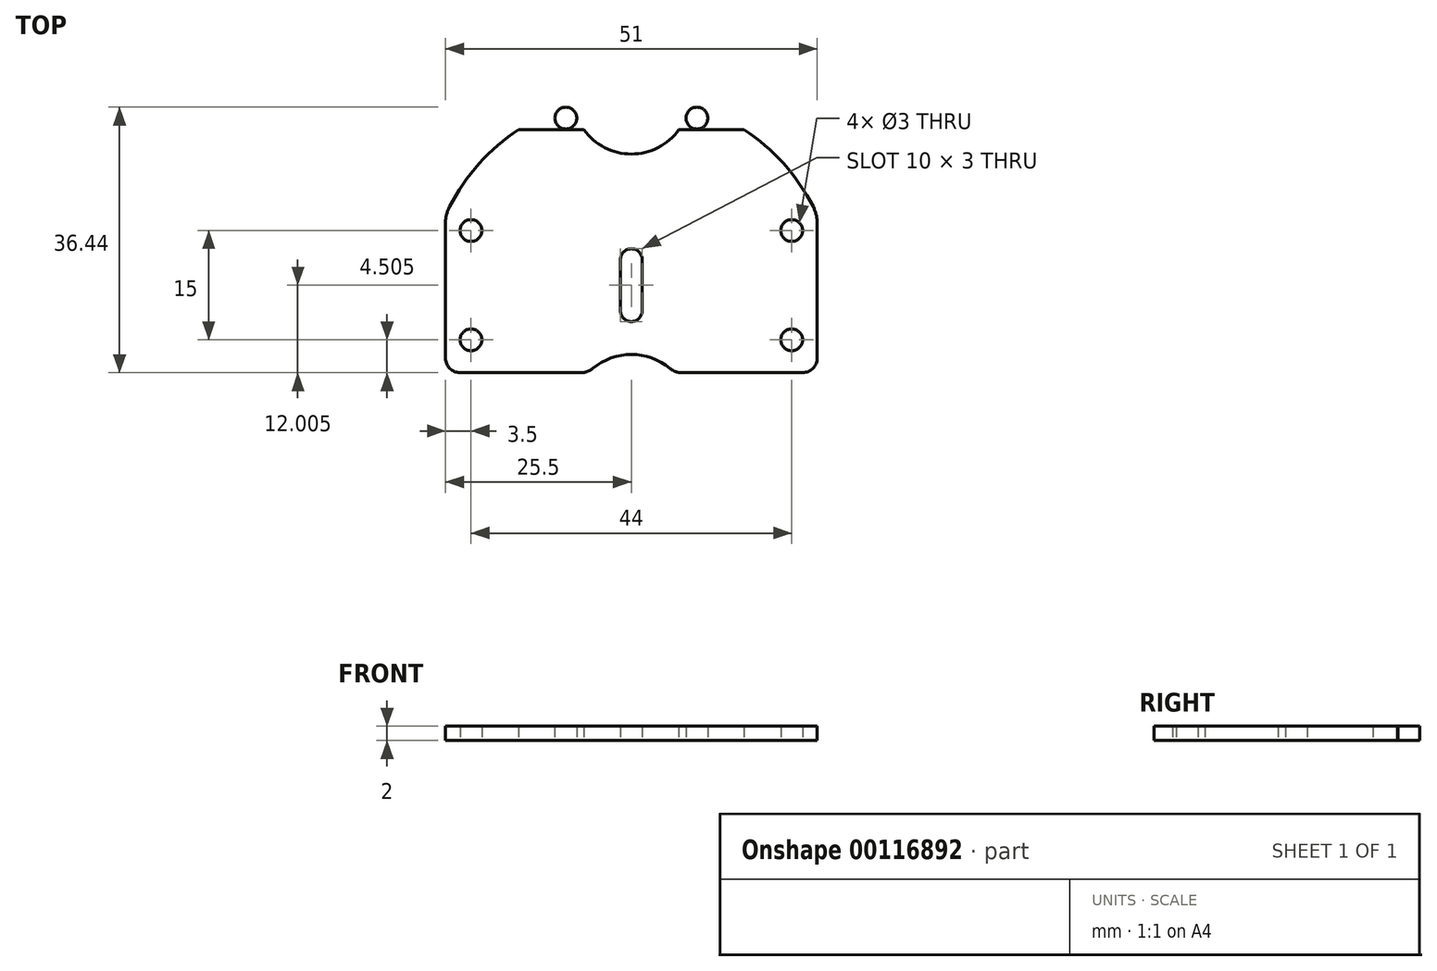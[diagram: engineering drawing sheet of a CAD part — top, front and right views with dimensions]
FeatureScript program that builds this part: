
annotation { "Feature Type Name" : "Feature", "Feature Type Description" : "" }
export const myFeature = defineFeature(function(context is Context, id is Id, definition is map)
    precondition{}
    {
        {
            var Q0;
            Q0=qCreatedBy(makeId("Top.planeOp"),FACE);
            var sketch = newSketch(context, id + "F0", { "sketchPlane" : qUnion([Q0])});
            skLineSegment(sketch, "E0", {"start": v(-27.15, 153.46) * mm, "end": v(-17.3, 155.2) * mm});
            skLineSegment(sketch, "E1", {"start": v(-17.3, 155.2) * mm, "end": v(-14.87, 141.4) * mm});
            skLineSegment(sketch, "E2", {"start": v(-14.87, 141.4) * mm, "end": v(-24.72, 139.67) * mm});
            skLineSegment(sketch, "E3", {"start": v(-24.72, 139.67) * mm, "end": v(-27.15, 153.46) * mm});
            skLineSegment(sketch, "E4", {"start": v(-8.87, 175.2) * mm, "end": v(-8.87, 29.62) * mm});
            skLineSegment(sketch, "E5", {"start": v(-63.87, 175.2) * mm, "end": v(-63.87, 29.62) * mm});
            skCircle(sketch, "E6", {"center": v(-17.3, 155.2) * mm, "radius": 1.43 * mm});
            skCircle(sketch, "E7", {"center": v(-27.15, 153.46) * mm, "radius": 1.43 * mm});
            skCircle(sketch, "E8", {"center": v(-24.72, 139.67) * mm, "radius": 1.43 * mm});
            skCircle(sketch, "E9", {"center": v(-14.87, 141.4) * mm, "radius": 1.43 * mm});
            skLineSegment(sketch, "E10", {"start": v(-63.87, 175.2) * mm, "end": v(-8.87, 175.2) * mm});
            skLineSegment(sketch, "E11", {"start": v(-45.6, 153.46) * mm, "end": v(-55.44, 155.2) * mm});
            skLineSegment(sketch, "E12", {"start": v(-55.44, 155.2) * mm, "end": v(-57.87, 141.4) * mm});
            skLineSegment(sketch, "E13", {"start": v(-57.87, 141.4) * mm, "end": v(-48.02, 139.67) * mm});
            skLineSegment(sketch, "E14", {"start": v(-48.02, 139.67) * mm, "end": v(-45.6, 153.46) * mm});
            skCircle(sketch, "E15", {"center": v(-55.44, 155.2) * mm, "radius": 1.43 * mm});
            skCircle(sketch, "E16", {"center": v(-45.6, 153.46) * mm, "radius": 1.43 * mm});
            skCircle(sketch, "E17", {"center": v(-48.02, 139.67) * mm, "radius": 1.43 * mm});
            skCircle(sketch, "E18", {"center": v(-57.87, 141.4) * mm, "radius": 1.43 * mm});
            skLineSegment(sketch, "E19", {"start": v(-36.37, 175.2) * mm, "end": v(-36.37, 125.26) * mm});
            skPoint(sketch, "E20", {"position": v(-36.37, 197.7) * mm});
            skArc(sketch, "E21", {"start": v(-11.42, 182.48) * mm, "mid": v(-36.37, 197.7) * mm, "end": v(-61.32, 182.48) * mm});
            skCircle(sketch, "E22", {"center": v(-36.37, 175.2) * mm, "radius": 1.5 * mm});
            skPoint(sketch, "E23.visualSharp", {"position": v(-63.87, 175.2) * mm});
            skPoint(sketch, "E24.visualSharp", {"position": v(-8.87, 175.2) * mm});
            skCircle(sketch, "E25", {"center": v(-58.87, 128.4) * mm, "radius": 1.5 * mm});
            skCircle(sketch, "E26.MirrorC", {"center": v(-13.87, 128.4) * mm, "radius": 1.5 * mm});
            skLineSegment(sketch, "E27", {"start": v(-48.87, 165.2) * mm, "end": v(-23.87, 165.2) * mm});
            skLineSegment(sketch, "E28", {"start": v(-53.87, 170.2) * mm, "end": v(-53.87, 191.57) * mm});
            skLineSegment(sketch, "E29", {"start": v(-18.87, 170.2) * mm, "end": v(-18.87, 191.57) * mm});
            skCircle(sketch, "E30", {"center": v(-56.37, 185.55) * mm, "radius": 2.5 * mm});
            skCircle(sketch, "E31", {"center": v(-16.37, 185.55) * mm, "radius": 2.5 * mm});
            skCircle(sketch, "E32", {"center": v(-58.37, 179.2) * mm, "radius": 1.5 * mm});
            skCircle(sketch, "E33", {"center": v(-14.37, 179.2) * mm, "radius": 1.5 * mm});
            skPoint(sketch, "E34.visualSharp", {"position": v(-53.87, 165.2) * mm});
            skArc(sketch, "E34.filletArc", {"start": v(-53.87, 170.2) * mm, "mid": v(-52.4, 166.66) * mm, "end": v(-48.87, 165.2) * mm});
            skPoint(sketch, "E35.visualSharp", {"position": v(-18.87, 165.2) * mm});
            skArc(sketch, "E35.filletArc", {"start": v(-23.87, 165.2) * mm, "mid": v(-20.33, 166.66) * mm, "end": v(-18.87, 170.2) * mm});
            skCircle(sketch, "E36", {"center": v(-36.37, 153.94) * mm, "radius": 3.25 * mm});
            skCircle(sketch, "E37", {"center": v(-46.8, 146.56) * mm, "radius": 1.43 * mm});
            skCircle(sketch, "E38.MirrorC", {"center": v(-25.93, 146.56) * mm, "radius": 1.43 * mm});
            skCircle(sketch, "E39", {"center": v(-58.37, 164.2) * mm, "radius": 1.5 * mm});
            skCircle(sketch, "E40", {"center": v(-14.37, 164.2) * mm, "radius": 1.5 * mm});
            skLineSegment(sketch, "E41", {"start": v(-61.87, 180.19) * mm, "end": v(-61.87, 161.7) * mm});
            skLineSegment(sketch, "E42", {"start": v(-59.87, 159.7) * mm, "end": v(-12.87, 159.7) * mm});
            skLineSegment(sketch, "E43", {"start": v(-10.87, 161.7) * mm, "end": v(-10.87, 180.19) * mm});
            skCircle(sketch, "E44", {"center": v(-36.37, 153.94) * mm, "radius": 8.25 * mm});
            skLineSegment(sketch, "E45", {"start": v(-58.78, 188.05) * mm, "end": v(-8.48, 188.05) * mm});
            skArc(sketch, "E46.filletArc", {"start": v(-61.32, 182.48) * mm, "mid": v(-61.73, 181.37) * mm, "end": v(-61.87, 180.19) * mm});
            skArc(sketch, "E47.filletArc", {"start": v(-10.87, 180.19) * mm, "mid": v(-11.01, 181.37) * mm, "end": v(-11.42, 182.48) * mm});
            skPoint(sketch, "E48.visualSharp", {"position": v(-10.87, 159.7) * mm});
            skArc(sketch, "E48.filletArc", {"start": v(-12.87, 159.7) * mm, "mid": v(-11.46, 160.28) * mm, "end": v(-10.87, 161.7) * mm});
            skPoint(sketch, "E49.visualSharp", {"position": v(-61.87, 159.7) * mm});
            skArc(sketch, "E49.filletArc", {"start": v(-61.87, 161.7) * mm, "mid": v(-61.28, 160.28) * mm, "end": v(-59.87, 159.7) * mm});
            skCircle(sketch, "E50", {"center": v(-43.26, 162.2) * mm, "radius": 2.5 * mm});
            skCircle(sketch, "E51", {"center": v(-29.48, 162.2) * mm, "radius": 2.5 * mm});
            skLineSegment(sketch, "E52", {"start": v(-59.41, 193.05) * mm, "end": v(-9.71, 193.05) * mm});
            skCircle(sketch, "E53", {"center": v(-36.37, 197.7) * mm, "radius": 8 * mm});
            skCircle(sketch, "E54", {"center": v(-45.36, 194.63) * mm, "radius": 1.5 * mm});
            skCircle(sketch, "E55", {"center": v(-27.38, 194.63) * mm, "radius": 1.5 * mm});
            skCircle(sketch, "E56", {"center": v(-36.37, 168.2) * mm, "radius": 1.5 * mm});
            skLineSegment(sketch, "E57", {"start": v(-37.87, 177.83) * mm, "end": v(-37.87, 165.8) * mm});
            skLineSegment(sketch, "E58", {"start": v(-34.87, 178) * mm, "end": v(-34.87, 166.07) * mm});
            skSolve(sketch);
        }
        {
            var Q0;
            {var subQ46=sQuery(id+"F0.wireOp",EDGE,"E4");Q0=makeQuery(id+"F0.imprint","IMPRINT",FACE,{"disambiguationData":[TD([[makeQuery(id+"F0.imprint","IMPRINT",EDGE,{"derivedFrom":subQ46}),-1.0]])]});}
            var Q1;
            Q1=makeQuery(id+"F0.imprint","IMPRINT",FACE,{"disambiguationData":[TD([[makeQuery(id+"F0.imprint","IMPRINT",EDGE,{"derivedFrom":sQuery(id+"F0.wireOp",EDGE,"0QWr4Jdi-5Swy-qNiu-C7BZ-pfZC10sv86ri")}),-1.0]])]});
            var Q2;
            {var subQ3=sQuery(id+"F0.wireOp",EDGE,"zpIQ2hdJ-70NU-OBih-8Bg3-goN3WX9r9ZsD");var subQ13=sQuery(id+"F0.wireOp",EDGE,"KCor8Cqw-w0U3-ZJtW-jTcY-G1uKAieuV0Lt");var subQ14=makeQuery(id+"F0.imprint","INTERSECT",VERTEX,{"derivedFrom":[subQ13,subQ3]});Q2=makeQuery(id+"F0.imprint","IMPRINT",FACE,{"disambiguationData":[TD([[makeQuery(id+"F0.imprint","IMPRINT",EDGE,{"disambiguationData":[TD([[subQ14,-1.0]])],"derivedFrom":subQ13}),-1.0]])]});}
            var Q3;
            {var subQ3=sQuery(id+"F0.wireOp",EDGE,"xyZ8QybP-hO6P-4geZ-8f6D-PIsMQULHAIPK");var subQ5=sQuery(id+"F0.wireOp",EDGE,"mBHuYMz8-ZQLY-wNrG-rzVk-AeopOfV37pT8");var subQ6=makeQuery(id+"F0.imprint","INTERSECT",VERTEX,{"derivedFrom":[subQ5,subQ3]});Q3=makeQuery(id+"F0.imprint","IMPRINT",FACE,{"disambiguationData":[TD([[makeQuery(id+"F0.imprint","IMPRINT",EDGE,{"disambiguationData":[TD([[subQ6,-1.0]])],"derivedFrom":subQ5}),-1.0]])]});}
            var Q4;
            Q4=makeQuery(id+"F0.imprint","IMPRINT",FACE,{"disambiguationData":[TD([[makeQuery(id+"F0.imprint","IMPRINT",EDGE,{"derivedFrom":sQuery(id+"F0.wireOp",EDGE,"0QWr4Jdi-5Swy-qNiu-C7BZ-pfZC10sv86ri")}),1.0]])]});
            var Q5;
            Q5=makeQuery(id+"F0.imprint","IMPRINT",FACE,{"disambiguationData":[TD([[makeQuery(id+"F0.imprint","IMPRINT",EDGE,{"derivedFrom":sQuery(id+"F0.wireOp",EDGE,"fiuo85jt-HlLJ-ANnF-wLPQ-esjs3jnNE0SC")}),1.0]])]});
            var Q6;
            Q6=makeQuery(id+"F0.imprint","IMPRINT",FACE,{"disambiguationData":[TD([[makeQuery(id+"F0.imprint","IMPRINT",EDGE,{"derivedFrom":sQuery(id+"F0.wireOp",EDGE,"nJGxZEk8-BIZM-s0Uf-ehRU-cHSEgP5oKWdw")}),1.0]])]});
            var Q7;
            Q7=makeQuery(id+"F0.imprint","IMPRINT",FACE,{"disambiguationData":[TD([[makeQuery(id+"F0.imprint","IMPRINT",EDGE,{"derivedFrom":sQuery(id+"F0.wireOp",EDGE,"yOxkreaX-tzGu-CvLJ-NVHy-oeYss2fHvc5B")}),1.0]])]});
            var Q8;
            {var subQ0=sQuery(id+"F0.wireOp",EDGE,"Asq052DE-T6gE-0AAR-ghXs-JX1L81zWd4of");var subQ1=sQuery(id+"F0.wireOp",EDGE,"mBHuYMz8-ZQLY-wNrG-rzVk-AeopOfV37pT8");var subQ2=makeQuery(id+"F0.imprint","INTERSECT",VERTEX,{"derivedFrom":[subQ1,subQ0]});Q8=makeQuery(id+"F0.imprint","IMPRINT",FACE,{"disambiguationData":[TD([[makeQuery(id+"F0.imprint","IMPRINT",EDGE,{"disambiguationData":[TD([[subQ2,-1.0]])],"derivedFrom":subQ1}),1.0]])]});}
            var Q9;
            {var subQ0=sQuery(id+"F0.wireOp",EDGE,"Asq052DE-T6gE-0AAR-ghXs-JX1L81zWd4of");var subQ1=sQuery(id+"F0.wireOp",EDGE,"mBHuYMz8-ZQLY-wNrG-rzVk-AeopOfV37pT8");var subQ2=makeQuery(id+"F0.imprint","INTERSECT",VERTEX,{"derivedFrom":[subQ1,subQ0]});Q9=makeQuery(id+"F0.imprint","IMPRINT",FACE,{"disambiguationData":[TD([[makeQuery(id+"F0.imprint","IMPRINT",EDGE,{"disambiguationData":[TD([[subQ2,-1.0]])],"derivedFrom":subQ1}),-1.0]])]});}
            var Q10;
            {var subQ0=sQuery(id+"F0.wireOp",EDGE,"Asq052DE-T6gE-0AAR-ghXs-JX1L81zWd4of");var subQ1=sQuery(id+"F0.wireOp",EDGE,"4mQizIiY-woOy-cA2D-KRvu-nd4lGExxEz3w");var subQ2=makeQuery(id+"F0.imprint","INTERSECT",VERTEX,{"derivedFrom":[subQ1,subQ0]});Q10=makeQuery(id+"F0.imprint","IMPRINT",FACE,{"disambiguationData":[TD([[makeQuery(id+"F0.imprint","IMPRINT",EDGE,{"disambiguationData":[TD([[subQ2,1.0]])],"derivedFrom":subQ1}),1.0]])]});}
            var Q11;
            {var subQ0=sQuery(id+"F0.wireOp",EDGE,"Asq052DE-T6gE-0AAR-ghXs-JX1L81zWd4of");var subQ1=sQuery(id+"F0.wireOp",EDGE,"4mQizIiY-woOy-cA2D-KRvu-nd4lGExxEz3w");var subQ2=makeQuery(id+"F0.imprint","INTERSECT",VERTEX,{"derivedFrom":[subQ1,subQ0]});Q11=makeQuery(id+"F0.imprint","IMPRINT",FACE,{"disambiguationData":[TD([[makeQuery(id+"F0.imprint","IMPRINT",EDGE,{"disambiguationData":[TD([[subQ2,1.0]])],"derivedFrom":subQ1}),-1.0]])]});}
            var Q12;
            {var subQ0=sQuery(id+"F0.wireOp",EDGE,"MDdCBIRf-hswZ-m4EO-fIZG-vuCMY65TxToA");var subQ1=sQuery(id+"F0.wireOp",EDGE,"KCor8Cqw-w0U3-ZJtW-jTcY-G1uKAieuV0Lt");var subQ2=makeQuery(id+"F0.imprint","INTERSECT",VERTEX,{"derivedFrom":[subQ1,subQ0]});Q12=makeQuery(id+"F0.imprint","IMPRINT",FACE,{"disambiguationData":[TD([[makeQuery(id+"F0.imprint","IMPRINT",EDGE,{"disambiguationData":[TD([[subQ2,1.0]])],"derivedFrom":subQ1}),1.0]])]});}
            var Q13;
            {var subQ0=sQuery(id+"F0.wireOp",EDGE,"MDdCBIRf-hswZ-m4EO-fIZG-vuCMY65TxToA");var subQ1=sQuery(id+"F0.wireOp",EDGE,"KCor8Cqw-w0U3-ZJtW-jTcY-G1uKAieuV0Lt");var subQ2=makeQuery(id+"F0.imprint","INTERSECT",VERTEX,{"derivedFrom":[subQ1,subQ0]});Q13=makeQuery(id+"F0.imprint","IMPRINT",FACE,{"disambiguationData":[TD([[makeQuery(id+"F0.imprint","IMPRINT",EDGE,{"disambiguationData":[TD([[subQ2,1.0]])],"derivedFrom":subQ1}),-1.0]])]});}
            var Q14;
            {var subQ0=sQuery(id+"F0.wireOp",EDGE,"8OitHLvR-Y0PI-VGHX-yggo-vIoiIR1Yse0j");var subQ1=sQuery(id+"F0.wireOp",EDGE,"MDdCBIRf-hswZ-m4EO-fIZG-vuCMY65TxToA");var subQ2=makeQuery(id+"F0.imprint","INTERSECT",VERTEX,{"derivedFrom":[subQ1,subQ0]});Q14=makeQuery(id+"F0.imprint","IMPRINT",FACE,{"disambiguationData":[TD([[makeQuery(id+"F0.imprint","IMPRINT",EDGE,{"disambiguationData":[TD([[subQ2,1.0]])],"derivedFrom":subQ1}),1.0]])]});}
            var Q15;
            {var subQ0=sQuery(id+"F0.wireOp",EDGE,"8OitHLvR-Y0PI-VGHX-yggo-vIoiIR1Yse0j");var subQ1=sQuery(id+"F0.wireOp",EDGE,"MDdCBIRf-hswZ-m4EO-fIZG-vuCMY65TxToA");var subQ2=makeQuery(id+"F0.imprint","INTERSECT",VERTEX,{"derivedFrom":[subQ1,subQ0]});Q15=makeQuery(id+"F0.imprint","IMPRINT",FACE,{"disambiguationData":[TD([[makeQuery(id+"F0.imprint","IMPRINT",EDGE,{"disambiguationData":[TD([[subQ2,1.0]])],"derivedFrom":subQ1}),-1.0]])]});}
            var Q16;
            {var subQ1=sQuery(id+"F0.wireOp",EDGE,"E10");var subQ3=sQuery(id+"F0.wireOp",EDGE,"E28");var subQ4=makeQuery(id+"F0.imprint","INTERSECT",VERTEX,{"derivedFrom":[subQ1,subQ3]});Q16=makeQuery(id+"F0.imprint","IMPRINT",FACE,{"disambiguationData":[TD([[makeQuery(id+"F0.imprint","IMPRINT",EDGE,{"disambiguationData":[TD([[subQ4,-1.0]])],"derivedFrom":subQ3}),1.0]])]});}
            var Q17;
            {var subQ0=sQuery(id+"F0.wireOp",EDGE,"E30");var subQ1=makeQuery(id+"F0.imprint","INTERSECT",VERTEX,{"derivedFrom":[sQuery(id+"F0.wireOp",EDGE,"E21"),subQ0]});Q17=makeQuery(id+"F0.imprint","IMPRINT",FACE,{"disambiguationData":[TD([[makeQuery(id+"F0.imprint","IMPRINT",EDGE,{"disambiguationData":[TD([[subQ1,1.0]])],"derivedFrom":subQ0}),1.0]])]});}
            var Q18;
            {var subQ1=sQuery(id+"F0.wireOp",EDGE,"E10");var subQ3=sQuery(id+"F0.wireOp",EDGE,"E29");var subQ4=makeQuery(id+"F0.imprint","INTERSECT",VERTEX,{"derivedFrom":[subQ1,subQ3]});Q18=makeQuery(id+"F0.imprint","IMPRINT",FACE,{"disambiguationData":[TD([[makeQuery(id+"F0.imprint","IMPRINT",EDGE,{"disambiguationData":[TD([[subQ4,-1.0]])],"derivedFrom":subQ3}),-1.0]])]});}
            var Q19;
            {var subQ0=sQuery(id+"F0.wireOp",EDGE,"E31");var subQ1=makeQuery(id+"F0.imprint","INTERSECT",VERTEX,{"derivedFrom":[sQuery(id+"F0.wireOp",EDGE,"E21"),subQ0]});Q19=makeQuery(id+"F0.imprint","IMPRINT",FACE,{"disambiguationData":[TD([[makeQuery(id+"F0.imprint","IMPRINT",EDGE,{"disambiguationData":[TD([[subQ1,-1.0]])],"derivedFrom":subQ0}),1.0]])]});}
            var Q20;
            {var subQ1=sQuery(id+"F0.wireOp",EDGE,"9PByZ2f5-CxSs-JYdf-CMjo-ML6Ht8AQyv0h");Q20=makeQuery(id+"F0.imprint","IMPRINT",FACE,{"disambiguationData":[TD([[makeQuery(id+"F0.imprint","IMPRINT",EDGE,{"derivedFrom":subQ1}),1.0]])]});}
            var Q21;
            {var subQ0=sQuery(id+"F0.wireOp",EDGE,"4c2edd1c-7cb4-4390-86bd-57d0a16ee9ce");Q21=makeQuery(id+"F0.imprint","IMPRINT",FACE,{"disambiguationData":[TD([[makeQuery(id+"F0.imprint","IMPRINT",EDGE,{"derivedFrom":subQ0}),1.0]])]});}
            var Q22;
            {var subQ0=sQuery(id+"F0.wireOp",EDGE,"abfb5665-3087-47af-a4d3-6f556c663ade0.MirrorCS");Q22=makeQuery(id+"F0.imprint","IMPRINT",FACE,{"disambiguationData":[TD([[makeQuery(id+"F0.imprint","IMPRINT",EDGE,{"derivedFrom":subQ0}),-1.0]])]});}
            var Q23;
            {var subQ1=sQuery(id+"F0.wireOp",EDGE,"E21");var subQ3=sQuery(id+"F0.wireOp",EDGE,"adHhhXEw-icbr-blXB-wO1p-EReYuO9yWeai");var subQ4=makeQuery(id+"F0.imprint","INTERSECT",VERTEX,{"derivedFrom":[subQ1,subQ3]});Q23=makeQuery(id+"F0.imprint","IMPRINT",FACE,{"disambiguationData":[TD([[makeQuery(id+"F0.imprint","IMPRINT",EDGE,{"disambiguationData":[TD([[subQ4,-1.0]])],"derivedFrom":subQ3}),1.0]])]});}
            var Q24;
            {var subQ1=sQuery(id+"F0.wireOp",EDGE,"E21");var subQ3=sQuery(id+"F0.wireOp",EDGE,"0PB8NEKn-i8lG-Bxgj-heOh-Yr0xhpc0avjP");var subQ4=makeQuery(id+"F0.imprint","INTERSECT",VERTEX,{"derivedFrom":[subQ1,subQ3]});Q24=makeQuery(id+"F0.imprint","IMPRINT",FACE,{"disambiguationData":[TD([[makeQuery(id+"F0.imprint","IMPRINT",EDGE,{"disambiguationData":[TD([[subQ4,-1.0]])],"derivedFrom":subQ3}),-1.0]])]});}
            var Q25;
            {var subQ7=sQuery(id+"F0.wireOp",EDGE,"E35.filletArc");Q25=makeQuery(id+"F0.imprint","IMPRINT",FACE,{"disambiguationData":[TD([[makeQuery(id+"F0.imprint","IMPRINT",EDGE,{"derivedFrom":subQ7}),1.0]])]});}
            var Q26;
            {var subQ0=sQuery(id+"F0.wireOp",EDGE,"E34.filletArc");Q26=makeQuery(id+"F0.imprint","IMPRINT",FACE,{"disambiguationData":[TD([[makeQuery(id+"F0.imprint","IMPRINT",EDGE,{"derivedFrom":subQ0}),1.0]])]});}
            var Q27;
            {var subQ0=sQuery(id+"F0.wireOp",EDGE,"E28");var subQ1=sQuery(id+"F0.wireOp",EDGE,"E10");var subQ2=makeQuery(id+"F0.imprint","INTERSECT",VERTEX,{"derivedFrom":[subQ1,subQ0]});Q27=makeQuery(id+"F0.imprint","IMPRINT",FACE,{"disambiguationData":[TD([[makeQuery(id+"F0.imprint","IMPRINT",EDGE,{"disambiguationData":[TD([[subQ2,-1.0]])],"derivedFrom":subQ1}),1.0]])]});}
            var Q28;
            {var subQ5=sQuery(id+"F0.wireOp",EDGE,"E34.filletArc");Q28=makeQuery(id+"F0.imprint","IMPRINT",FACE,{"disambiguationData":[TD([[makeQuery(id+"F0.imprint","IMPRINT",EDGE,{"derivedFrom":subQ5}),-1.0]])]});}
            var Q29;
            {var subQ0=sQuery(id+"F0.wireOp",EDGE,"E50");var subQ1=makeQuery(id+"F0.imprint","INTERSECT",VERTEX,{"derivedFrom":[sQuery(id+"F0.wireOp",EDGE,"E42"),subQ0]});Q29=makeQuery(id+"F0.imprint","IMPRINT",FACE,{"disambiguationData":[TD([[makeQuery(id+"F0.imprint","IMPRINT",EDGE,{"disambiguationData":[TD([[subQ1,-1.0]])],"derivedFrom":subQ0}),1.0]])]});}
            var Q30;
            {var subQ0=sQuery(id+"F0.wireOp",EDGE,"E30");var subQ1=sQuery(id+"F0.wireOp",EDGE,"E28");var subQ2=makeQuery(id+"F0.imprint","INTERSECT",VERTEX,{"derivedFrom":[subQ1,subQ0]});Q30=makeQuery(id+"F0.imprint","IMPRINT",FACE,{"disambiguationData":[TD([[makeQuery(id+"F0.imprint","IMPRINT",EDGE,{"disambiguationData":[TD([[subQ2,-1.0]])],"derivedFrom":subQ1}),1.0]])]});}
            var Q31;
            {var subQ0=sQuery(id+"F0.wireOp",EDGE,"E31");var subQ1=sQuery(id+"F0.wireOp",EDGE,"E29");var subQ2=makeQuery(id+"F0.imprint","INTERSECT",VERTEX,{"derivedFrom":[subQ1,subQ0]});Q31=makeQuery(id+"F0.imprint","IMPRINT",FACE,{"disambiguationData":[TD([[makeQuery(id+"F0.imprint","IMPRINT",EDGE,{"disambiguationData":[TD([[subQ2,-1.0]])],"derivedFrom":subQ1}),-1.0]])]});}
            var Q32;
            {var subQ15=sQuery(id+"F0.wireOp",EDGE,"E35.filletArc");Q32=makeQuery(id+"F0.imprint","IMPRINT",FACE,{"disambiguationData":[TD([[makeQuery(id+"F0.imprint","IMPRINT",EDGE,{"derivedFrom":subQ15}),-1.0]])]});}
            var Q33;
            {var subQ0=sQuery(id+"F0.wireOp",EDGE,"E51");var subQ1=makeQuery(id+"F0.imprint","INTERSECT",VERTEX,{"derivedFrom":[sQuery(id+"F0.wireOp",EDGE,"E42"),subQ0]});Q33=makeQuery(id+"F0.imprint","IMPRINT",FACE,{"disambiguationData":[TD([[makeQuery(id+"F0.imprint","IMPRINT",EDGE,{"disambiguationData":[TD([[subQ1,1.0]])],"derivedFrom":subQ0}),1.0]])]});}
            var Q34;
            {var subQ0=sQuery(id+"F0.wireOp",EDGE,"E29");var subQ1=sQuery(id+"F0.wireOp",EDGE,"E21");var subQ2=makeQuery(id+"F0.imprint","INTERSECT",VERTEX,{"derivedFrom":[subQ1,subQ0]});Q34=makeQuery(id+"F0.imprint","IMPRINT",FACE,{"disambiguationData":[TD([[makeQuery(id+"F0.imprint","IMPRINT",EDGE,{"disambiguationData":[TD([[subQ2,-1.0]])],"derivedFrom":subQ1}),1.0]])]});}
            var Q35;
            {var subQ0=sQuery(id+"F0.wireOp",EDGE,"E28");var subQ1=sQuery(id+"F0.wireOp",EDGE,"E21");var subQ2=makeQuery(id+"F0.imprint","INTERSECT",VERTEX,{"derivedFrom":[subQ1,subQ0]});Q35=makeQuery(id+"F0.imprint","IMPRINT",FACE,{"disambiguationData":[TD([[makeQuery(id+"F0.imprint","IMPRINT",EDGE,{"disambiguationData":[TD([[subQ2,-1.0]])],"derivedFrom":subQ1}),1.0]])]});}
            var Q36;
            {var subQ0=sQuery(id+"F0.wireOp",EDGE,"E29");var subQ1=sQuery(id+"F0.wireOp",EDGE,"E21");var subQ2=makeQuery(id+"F0.imprint","INTERSECT",VERTEX,{"derivedFrom":[subQ1,subQ0]});Q36=makeQuery(id+"F0.imprint","IMPRINT",FACE,{"disambiguationData":[TD([[makeQuery(id+"F0.imprint","IMPRINT",EDGE,{"disambiguationData":[TD([[subQ2,1.0]])],"derivedFrom":subQ1}),1.0]])]});}
            var Q37;
            {var subQ0=sQuery(id+"F0.wireOp",EDGE,"E45");var subQ1=sQuery(id+"F0.wireOp",EDGE,"E21");var subQ2=makeQuery(id+"F0.imprint","INTERSECT",VERTEX,{"disambiguationData":[OD(1.0)],"derivedFrom":[subQ1,subQ0]});Q37=makeQuery(id+"F0.imprint","IMPRINT",FACE,{"disambiguationData":[TD([[makeQuery(id+"F0.imprint","IMPRINT",EDGE,{"disambiguationData":[TD([[subQ2,-1.0]])],"derivedFrom":subQ1}),1.0]])]});}
            var Q38;
            {var subQ0=sQuery(id+"F0.wireOp",EDGE,"E45");var subQ1=sQuery(id+"F0.wireOp",EDGE,"E21");var subQ2=makeQuery(id+"F0.imprint","INTERSECT",VERTEX,{"disambiguationData":[OD(0.0)],"derivedFrom":[subQ1,subQ0]});Q38=makeQuery(id+"F0.imprint","IMPRINT",FACE,{"disambiguationData":[TD([[makeQuery(id+"F0.imprint","IMPRINT",EDGE,{"disambiguationData":[TD([[subQ2,1.0]])],"derivedFrom":subQ1}),1.0]])]});}
            var Q39;
            {var subQ0=sQuery(id+"F0.wireOp",EDGE,"E52");var subQ1=sQuery(id+"F0.wireOp",EDGE,"E21");var subQ2=makeQuery(id+"F0.imprint","INTERSECT",VERTEX,{"disambiguationData":[OD(0.0)],"derivedFrom":[subQ1,subQ0]});Q39=makeQuery(id+"F0.imprint","IMPRINT",FACE,{"disambiguationData":[TD([[makeQuery(id+"F0.imprint","IMPRINT",EDGE,{"disambiguationData":[TD([[subQ2,-1.0]])],"derivedFrom":subQ1}),1.0]])]});}
            var Q40;
            {var subQ0=sQuery(id+"F0.wireOp",EDGE,"E55");var subQ1=makeQuery(id+"F0.imprint","INTERSECT",VERTEX,{"derivedFrom":[sQuery(id+"F0.wireOp",EDGE,"E21"),subQ0]});Q40=makeQuery(id+"F0.imprint","IMPRINT",FACE,{"disambiguationData":[TD([[makeQuery(id+"F0.imprint","IMPRINT",EDGE,{"disambiguationData":[TD([[subQ1,-1.0]])],"derivedFrom":subQ0}),1.0]])]});}
            var Q41;
            {var subQ0=sQuery(id+"F0.wireOp",EDGE,"E54");var subQ1=makeQuery(id+"F0.imprint","INTERSECT",VERTEX,{"derivedFrom":[sQuery(id+"F0.wireOp",EDGE,"E21"),subQ0]});Q41=makeQuery(id+"F0.imprint","IMPRINT",FACE,{"disambiguationData":[TD([[makeQuery(id+"F0.imprint","IMPRINT",EDGE,{"disambiguationData":[TD([[subQ1,1.0]])],"derivedFrom":subQ0}),1.0]])]});}
            var Q42;
            {var subQ0=sQuery(id+"F0.wireOp",EDGE,"E52");var subQ1=sQuery(id+"F0.wireOp",EDGE,"E21");var subQ2=makeQuery(id+"F0.imprint","INTERSECT",VERTEX,{"disambiguationData":[OD(1.0)],"derivedFrom":[subQ1,subQ0]});Q42=makeQuery(id+"F0.imprint","IMPRINT",FACE,{"disambiguationData":[TD([[makeQuery(id+"F0.imprint","IMPRINT",EDGE,{"disambiguationData":[TD([[subQ2,1.0]])],"derivedFrom":subQ1}),1.0]])]});}
            extrude(context, id + "F1", {"entities" : qUnion([Q0, Q1, Q2, Q3, Q4, Q5, Q6, Q7, Q8, Q9, Q10, Q11, Q12, Q13, Q14, Q15, Q16, Q17, Q18, Q19, Q20, Q21, Q22, Q23, Q24, Q25, Q26, Q27, Q28, Q29, Q30, Q31, Q32, Q33, Q34, Q35, Q36, Q37, Q38, Q39, Q40, Q41, Q42]), "depth" : 2 * mm});
        }
    });
